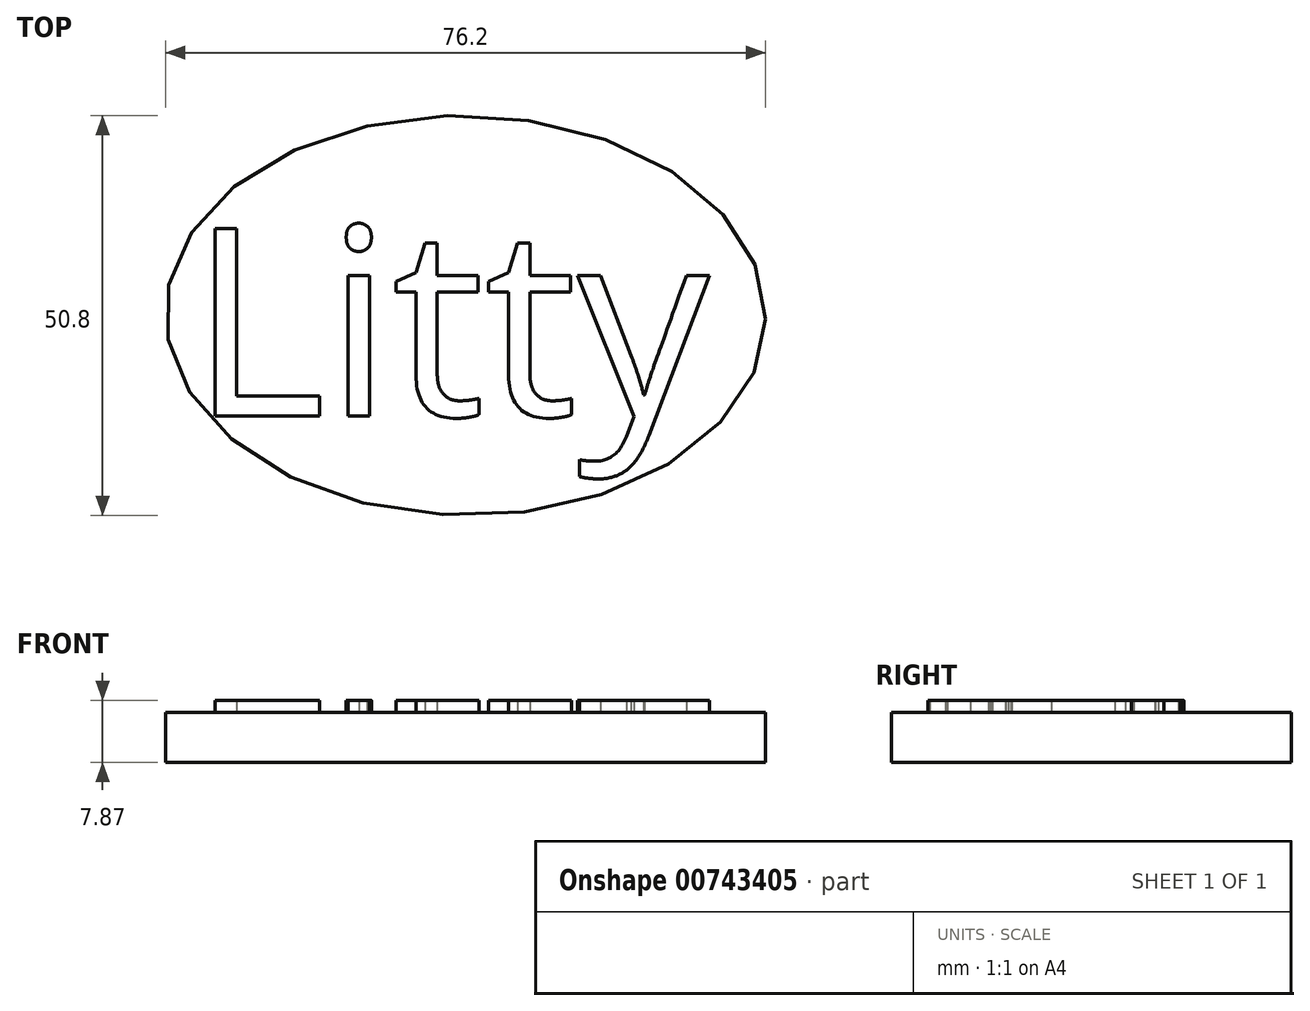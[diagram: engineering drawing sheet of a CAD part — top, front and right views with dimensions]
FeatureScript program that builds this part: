
annotation { "Feature Type Name" : "Feature", "Feature Type Description" : "" }
export const myFeature = defineFeature(function(context is Context, id is Id, definition is map)
    precondition{}
    {
        {
            var Q0;
            Q0=qCreatedBy(makeId("Top.planeOp"),FACE);
            var sketch = newSketch(context, id + "F0", { "sketchPlane" : qUnion([Q0])});
            skEllipse(sketch, "E0", {"center": v(0, 0) * mm, "majorRadius": 38.1 * mm, "minorRadius": 25.4 * mm, "majorAxis": v(1, -0.01)});
            skSolve(sketch);
        }
        {
            var Q0;
            Q0 = qSketchRegion(id + "F0", true);
            extrude(context, id + "F1", {"entities" : qUnion([Q0]), "depth" : 6.35 * mm, "offsetDistance" : 25.4 * mm});
        }
        {
            var Q0;
            Q0=makeQuery(id+"F1.opExtrude","CAP_FACE",FACE,{"disambiguationData":[OSD([sQuery(id+"F0.wireOp",EDGE,"E0")])],"isStart":false});
            var sketch = newSketch(context, id + "F2", { "sketchPlane" : qUnion([Q0])});
            skText(sketch, "E1", { "text": "Litty", "fontName": "OpenSans-Regular.ttf"});
            const initialGuessF2  = {"E1": [-0.0351, -0.01275, 1, 0, 0.02401]};
            skSetInitialGuess(sketch, initialGuessF2);
            skSolve(sketch);
        }
        {
            var Q0;
            Q0 = qSketchRegion(id + "F2", true);
            extrude(context, id + "F3", {"entities" : qUnion([Q0]), "operationType" : NewBodyOperationType.ADD, "depth" : 1.52 * mm, "offsetDistance" : 25.4 * mm});
        }
    });
